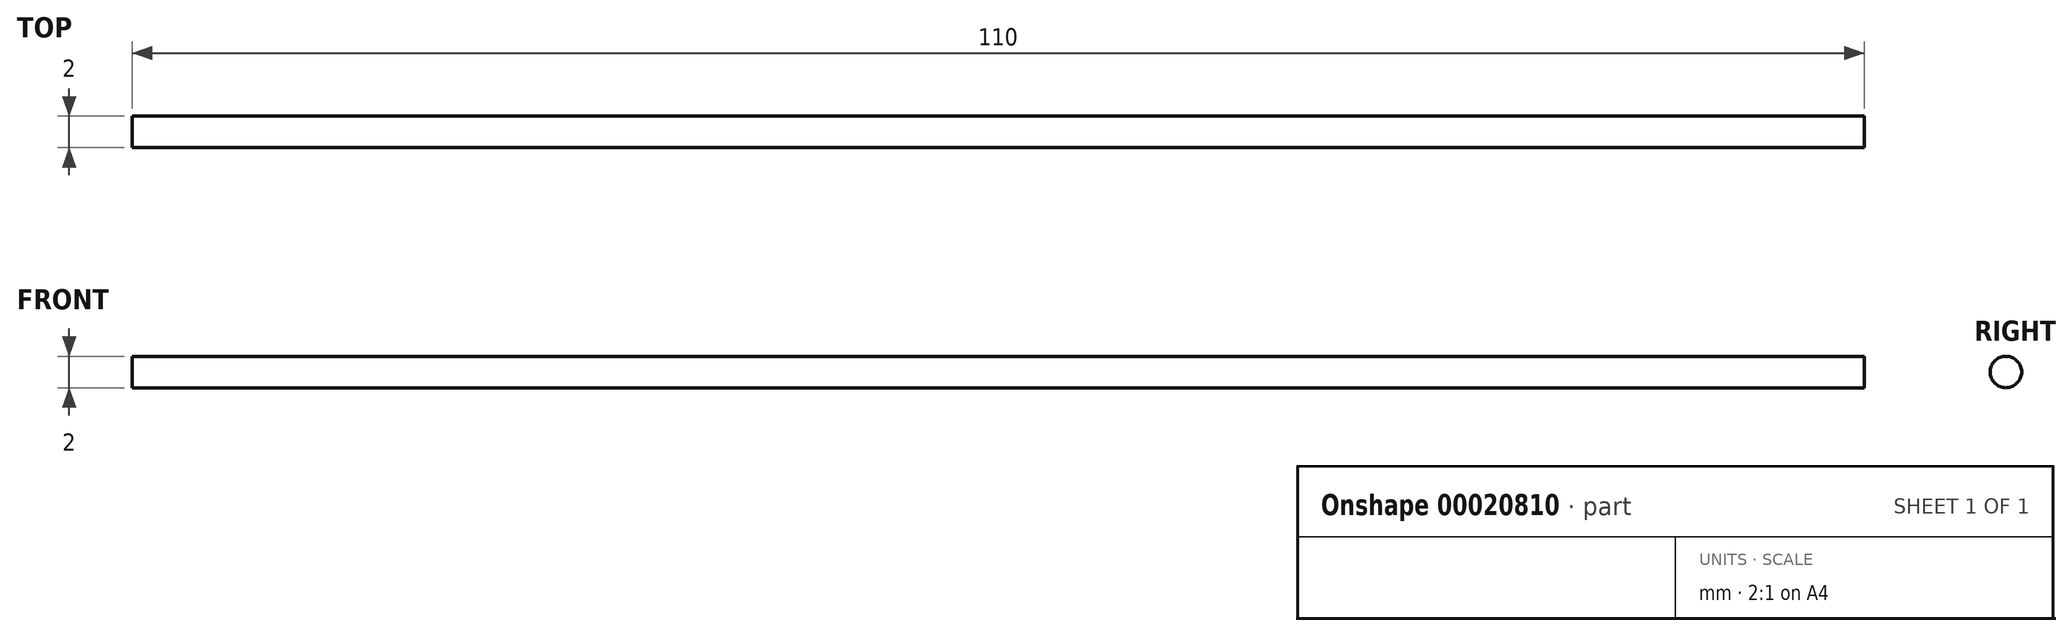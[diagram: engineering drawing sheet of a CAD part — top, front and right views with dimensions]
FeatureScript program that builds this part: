
annotation { "Feature Type Name" : "Feature", "Feature Type Description" : "" }
export const myFeature = defineFeature(function(context is Context, id is Id, definition is map)
    precondition{}
    {
        {
            var Q0;
            Q0=qCreatedBy(makeId("Right.planeOp"),FACE);
            var sketch = newSketch(context, id + "F0", { "sketchPlane" : qUnion([Q0])});
            skCircle(sketch, "E0", {"center": v(0, 0) * mm, "radius": 1 * mm});
            skSolve(sketch);
        }
        {
            var Q0;
            Q0 = qSketchRegion(id + "F0", true);
            extrude(context, id + "F1", {"entities" : qUnion([Q0]), "depth" : 110 * mm});
        }
    });
